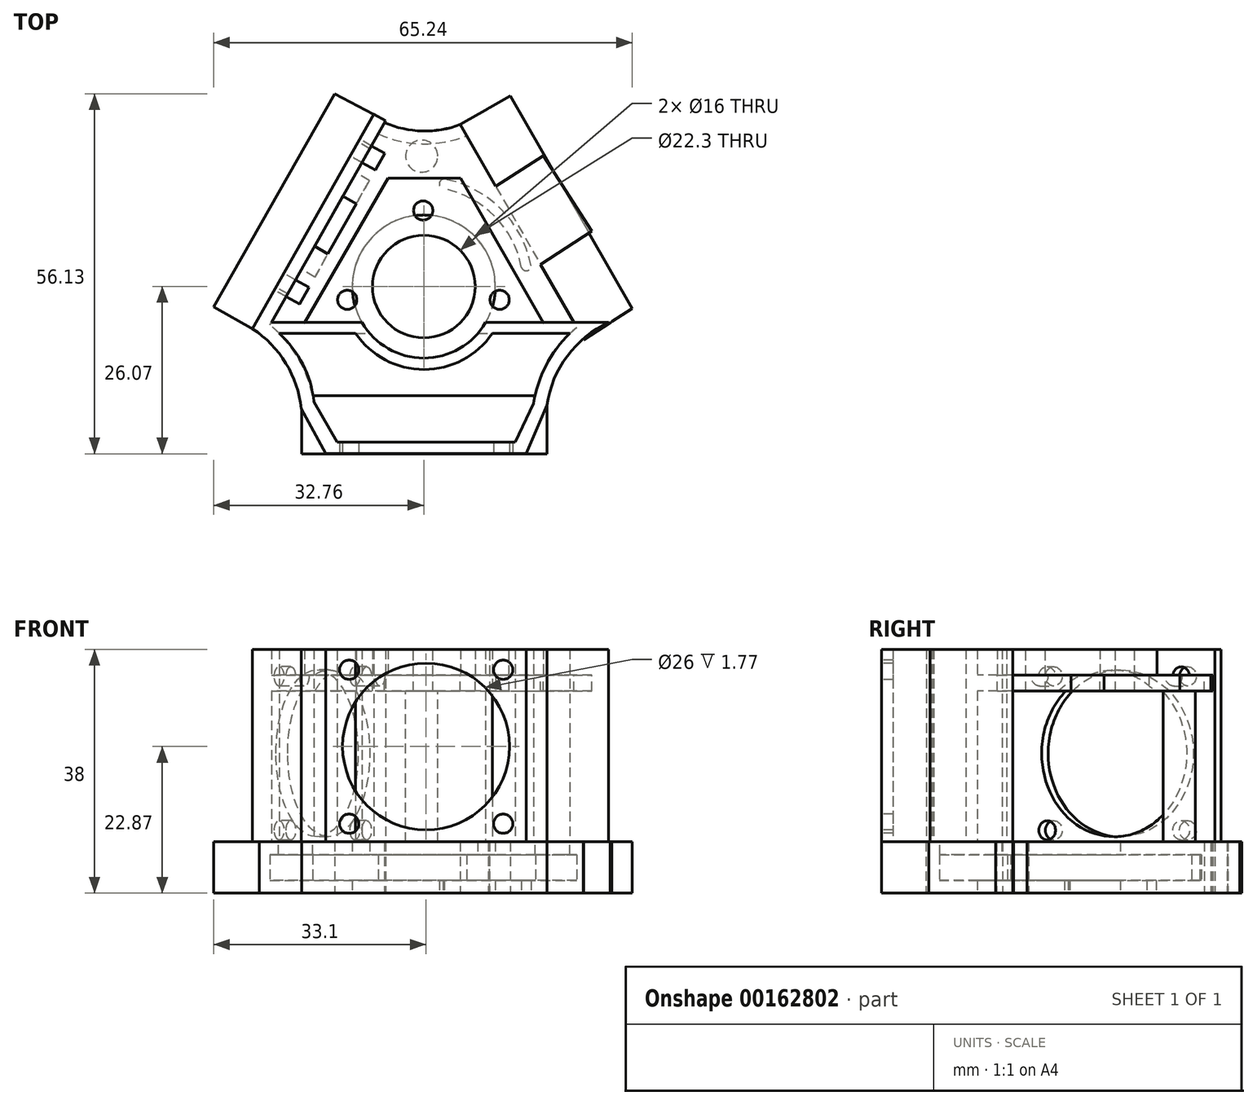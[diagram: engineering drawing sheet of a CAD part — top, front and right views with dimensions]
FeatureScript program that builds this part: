
annotation { "Feature Type Name" : "Feature", "Feature Type Description" : "" }
export const myFeature = defineFeature(function(context is Context, id is Id, definition is map)
    precondition{}
    {
        {
            var Q0;
            Q0=qCreatedBy(makeId("Top.planeOp"),FACE);
            var sketch = newSketch(context, id + "F0", { "sketchPlane" : qUnion([Q0])});
            skLineSegment(sketch, "E0", {"start": v(-28.93, -4.72) * mm, "end": v(-9.95, 28.39) * mm});
            skLineSegment(sketch, "E1", {"start": v(10.22, 28.39) * mm, "end": v(29.31, -5.05) * mm});
            skLineSegment(sketch, "E2", {"start": v(19.17, -21.87) * mm, "end": v(-19, -21.87) * mm});
            skArc(sketch, "E3", {"start": v(-9.95, 28.39) * mm, "mid": v(0.14, 24.72) * mm, "end": v(10.22, 28.39) * mm});
            skArc(sketch, "E4", {"start": v(-19, -21.87) * mm, "mid": v(-21.28, -11.74) * mm, "end": v(-28.93, -4.72) * mm});
            skArc(sketch, "E5", {"start": v(29.31, -5.05) * mm, "mid": v(21.38, -11.73) * mm, "end": v(19.17, -21.87) * mm});
            skSolve(sketch);
        }
        {
            var Q0;
            Q0 = qSketchRegion(id + "F0", true);
            extrude(context, id + "F1", {"entities" : qUnion([Q0]), "depth" : 8 * mm});
        }
        {
            var Q0;
            Q0=makeQuery(id+"F1.opExtrude","CAP_FACE",FACE,{"disambiguationData":[OSD([sQuery(id+"F0.wireOp",EDGE,"E0"),sQuery(id+"F0.wireOp",EDGE,"E1"),sQuery(id+"F0.wireOp",EDGE,"E2"),sQuery(id+"F0.wireOp",EDGE,"E3"),sQuery(id+"F0.wireOp",EDGE,"E4"),sQuery(id+"F0.wireOp",EDGE,"E5")])],"isStart":false});
            var Q1;
            Q1=makeQuery(id+"F1.opExtrude","SWEPT_BODY",BODY,{"disambiguationData":[OSD([sQuery(id+"F0.wireOp",EDGE,"E0"),sQuery(id+"F0.wireOp",EDGE,"E1"),sQuery(id+"F0.wireOp",EDGE,"E2"),sQuery(id+"F0.wireOp",EDGE,"E3"),sQuery(id+"F0.wireOp",EDGE,"E4"),sQuery(id+"F0.wireOp",EDGE,"E5")])]});
            shell(context, id + "F2", {"isHollow" : true, "entities" : qUnion([Q0]), "parts" : qUnion([Q1]), "thickness" : 2 * mm});
        }
        {
            var Q0;
            Q0=qCreatedBy(makeId("Top.planeOp"),FACE);
            var sketch = newSketch(context, id + "F3", { "sketchPlane" : qUnion([Q0])});
            skCircle(sketch, "E6", {"center": v(0, 0.47) * mm, "radius": 11.15 * mm});
            skSolve(sketch);
        }
        {
            var Q0;
            Q0 = qSketchRegion(id + "F3", true);
            extrude(context, id + "F4", {"entities" : qUnion([Q0]), "operationType" : NewBodyOperationType.REMOVE, "depth" : 8 * mm});
        }
        {
            var Q0;
            Q0=qCreatedBy(makeId("Top.planeOp"),FACE);
            var sketch = newSketch(context, id + "F5", { "sketchPlane" : qUnion([Q0])});
            skLineSegment(sketch, "E7.bottom", {"start": v(-19.03, -25.6) * mm, "end": v(19.17, -25.6) * mm});
            skLineSegment(sketch, "E7.top", {"start": v(-19.03, -16.6) * mm, "end": v(19.17, -16.6) * mm});
            skLineSegment(sketch, "E7.left", {"start": v(-19.03, -25.6) * mm, "end": v(-19.03, -16.6) * mm});
            skLineSegment(sketch, "E7.right", {"start": v(19.17, -25.6) * mm, "end": v(19.17, -16.6) * mm});
            skLineSegment(sketch, "E8", {"start": v(-5.95, 26.32) * mm, "end": v(-24.93, -7.14) * mm});
            skLineSegment(sketch, "E9", {"start": v(-24.93, -7.14) * mm, "end": v(-32.76, -2.7) * mm});
            skLineSegment(sketch, "E10", {"start": v(-32.76, -2.7) * mm, "end": v(-13.9, 30.53) * mm});
            skLineSegment(sketch, "E11", {"start": v(-13.9, 30.53) * mm, "end": v(-5.95, 26.32) * mm});
            skLineSegment(sketch, "E12", {"start": v(24.9, -7.82) * mm, "end": v(5.68, 25.75) * mm});
            skLineSegment(sketch, "E13", {"start": v(5.68, 25.75) * mm, "end": v(13.5, 30.22) * mm});
            skLineSegment(sketch, "E14", {"start": v(13.5, 30.22) * mm, "end": v(32.48, -2.93) * mm});
            skLineSegment(sketch, "E15", {"start": v(32.48, -2.93) * mm, "end": v(24.9, -7.82) * mm});
            skSolve(sketch);
        }
        {
            var Q0;
            Q0 = qSketchRegion(id + "F5", true);
            extrude(context, id + "F6", {"entities" : qUnion([Q0]), "operationType" : NewBodyOperationType.ADD, "depth" : 8 * mm});
        }
        {
            var Q0;
            Q0=qCreatedBy(makeId("Top.planeOp"),FACE);
            var sketch = newSketch(context, id + "F7", { "sketchPlane" : qUnion([Q0])});
            skArc(sketch, "E16", {"start": v(-3.14, 15.7) * mm, "mid": v(-11.4, 11.03) * mm, "end": v(-15.39, 2.41) * mm});
            skArc(sketch, "E17", {"start": v(-3.35, 17.2) * mm, "mid": v(-12.43, 12.13) * mm, "end": v(-16.86, 2.72) * mm});
            skArc(sketch, "E18", {"start": v(-3.68, -16.07) * mm, "mid": v(-2.82, -15.38) * mm, "end": v(-3.56, -14.55) * mm});
            skArc(sketch, "E19", {"start": v(3.62, -14.54) * mm, "mid": v(3.02, -15.33) * mm, "end": v(3.68, -16.07) * mm});
            skArc(sketch, "E20", {"start": v(-15.18, -2.6) * mm, "mid": v(-16.03, -2) * mm, "end": v(-16.67, -2.83) * mm});
            skArc(sketch, "E21", {"start": v(-16.86, 2.72) * mm, "mid": v(-16.08, 1.92) * mm, "end": v(-15.34, 2.76) * mm});
            skArc(sketch, "E22", {"start": v(16.53, -3.44) * mm, "mid": v(15.9, -2.57) * mm, "end": v(15.04, -3.22) * mm});
            skArc(sketch, "E23", {"start": v(15.22, 3.48) * mm, "mid": v(16.07, 2.94) * mm, "end": v(16.7, 3.73) * mm});
            skArc(sketch, "E24", {"start": v(-3.14, 15.7) * mm, "mid": v(-2.68, 16.53) * mm, "end": v(-3.35, 17.2) * mm});
            skArc(sketch, "E25", {"start": v(3.16, 17.23) * mm, "mid": v(2.41, 16.56) * mm, "end": v(2.99, 15.74) * mm});
            skArc(sketch, "E26.trimOffspring", {"start": v(-15.18, -2.59) * mm, "mid": v(-11, -10.38) * mm, "end": v(-3.26, -14.62) * mm});
            skArc(sketch, "E27.trimOffspring", {"start": v(-16.67, -2.83) * mm, "mid": v(-12.14, -11.37) * mm, "end": v(-3.68, -16.07) * mm});
            skArc(sketch, "E28.trimOffspring", {"start": v(16.7, 3.73) * mm, "mid": v(12, 12.57) * mm, "end": v(3.16, 17.23) * mm});
            skArc(sketch, "E29.trimOffspring", {"start": v(15.22, 3.48) * mm, "mid": v(10.98, 11.48) * mm, "end": v(2.99, 15.74) * mm});
            skArc(sketch, "E30.trimOffspring", {"start": v(3.62, -14.54) * mm, "mid": v(10.97, -10.42) * mm, "end": v(15.08, -3.06) * mm});
            skArc(sketch, "E31.trimOffspring", {"start": v(3.68, -16.07) * mm, "mid": v(11.92, -11.6) * mm, "end": v(16.53, -3.44) * mm});
            skSolve(sketch);
        }
        {
            var Q0;
            Q0 = qSketchRegion(id + "F7", true);
            extrude(context, id + "F8", {"entities" : qUnion([Q0]), "operationType" : NewBodyOperationType.REMOVE, "depth" : 2 * mm});
        }
        {
            var Q0;
            Q0=qCreatedBy(makeId("Top.planeOp"),FACE);
            cPlane(context, id + "F9", {"entities" : qUnion([Q0]), "cplaneType" : CPlaneType.OFFSET, "offset" : 8 * mm, "width" : 150 * mm, "height" : 150 * mm});
        }
        {
            var Q0;
            Q0=qCreatedBy(id+"F9.planeOp",FACE);
            var sketch = newSketch(context, id + "F10", { "sketchPlane" : qUnion([Q0])});
            skLineSegment(sketch, "E32.bottom", {"start": v(-22.63, -6.84) * mm, "end": v(22.76, -6.84) * mm});
            skLineSegment(sketch, "E32.top", {"start": v(-17.3, -16.53) * mm, "end": v(17.36, -16.53) * mm});
            skArc(sketch, "E33", {"start": v(-17.3, -16.53) * mm, "mid": v(-19.12, -11.22) * mm, "end": v(-22.63, -6.84) * mm});
            skArc(sketch, "E34", {"start": v(22.76, -6.84) * mm, "mid": v(19.34, -11.29) * mm, "end": v(17.36, -16.53) * mm});
            skSolve(sketch);
        }
        {
            var Q0;
            Q0 = qSketchRegion(id + "F10", true);
            extrude(context, id + "F11", {"entities" : qUnion([Q0]), "operationType" : NewBodyOperationType.REMOVE, "oppositeDirection" : true, "depth" : 2 * mm});
        }
        {
            var Q0;
            Q0=qCreatedBy(id+"F9.planeOp",FACE);
            var sketch = newSketch(context, id + "F12", { "sketchPlane" : qUnion([Q0])});
            skLineSegment(sketch, "E35", {"start": v(-23.76, -5.14) * mm, "end": v(-9.62, -5.14) * mm});
            skLineSegment(sketch, "E36", {"start": v(15.94, -25.57) * mm, "end": v(-15.28, -25.57) * mm});
            skLineSegment(sketch, "E37", {"start": v(19.18, -18.03) * mm, "end": v(15.94, -25.57) * mm});
            skLineSegment(sketch, "E38", {"start": v(-19.07, -18.6) * mm, "end": v(-15.28, -25.57) * mm});
            skArc(sketch, "E39", {"start": v(-9.62, -5.14) * mm, "mid": v(0, -10.69) * mm, "end": v(9.62, -5.14) * mm});
            skLineSegment(sketch, "E40.trimOffspring", {"start": v(9.62, -5.14) * mm, "end": v(28.8, -5.14) * mm});
            skArc(sketch, "E41", {"start": v(28.8, -5.14) * mm, "mid": v(22.35, -10.36) * mm, "end": v(19.18, -18.03) * mm});
            skLineSegment(sketch, "E42", {"start": v(-22.56, -6.83) * mm, "end": v(-10.63, -6.83) * mm});
            skArc(sketch, "E43", {"start": v(22.75, -6.83) * mm, "mid": v(19.04, -11.82) * mm, "end": v(17.1, -17.73) * mm});
            skArc(sketch, "E44", {"start": v(-17.11, -17.48) * mm, "mid": v(-18.87, -11.66) * mm, "end": v(-22.56, -6.83) * mm});
            skArc(sketch, "E45", {"start": v(-10.63, -6.83) * mm, "mid": v(0.02, -12.46) * mm, "end": v(10.67, -6.83) * mm});
            skLineSegment(sketch, "E46.trimOffspring", {"start": v(10.67, -6.83) * mm, "end": v(22.75, -6.83) * mm});
            skLineSegment(sketch, "E47", {"start": v(-13.5, -23.8) * mm, "end": v(14.25, -23.8) * mm});
            skLineSegment(sketch, "E48", {"start": v(14.25, -23.8) * mm, "end": v(17.1, -17.73) * mm});
            skLineSegment(sketch, "E49", {"start": v(-13.5, -23.8) * mm, "end": v(-17.11, -17.48) * mm});
            skLineSegment(sketch, "E50", {"start": v(-23.76, -5.14) * mm, "end": v(-5.95, 26.32) * mm});
            skLineSegment(sketch, "E51", {"start": v(-5.95, 26.32) * mm, "end": v(-7.83, 27.32) * mm});
            skLineSegment(sketch, "E52", {"start": v(-7.83, 27.32) * mm, "end": v(-26.7, -6.11) * mm});
            skArc(sketch, "E53", {"start": v(-19.07, -18.6) * mm, "mid": v(-21.5, -11.5) * mm, "end": v(-26.7, -6.11) * mm});
            skSolve(sketch);
        }
        {
            var Q0;
            Q0 = qSketchRegion(id + "F12", true);
            extrude(context, id + "F13", {"entities" : qUnion([Q0]), "operationType" : NewBodyOperationType.ADD, "depth" : 30 * mm});
        }
        {
            var Q0;
            Q0=qCreatedBy(makeId("Top.planeOp"),FACE);
            cPlane(context, id + "F14", {"entities" : qUnion([Q0]), "cplaneType" : CPlaneType.OFFSET, "offset" : 38 * mm, "width" : 150 * mm, "height" : 150 * mm});
        }
        {
            var Q0;
            Q0=qCreatedBy(id+"F14.planeOp",FACE);
            var sketch = newSketch(context, id + "F15", { "sketchPlane" : qUnion([Q0])});
            skLineSegment(sketch, "E54", {"start": v(24.75, -7.55) * mm, "end": v(24.83, -7.7) * mm});
            skLineSegment(sketch, "E55", {"start": v(24.83, -7.7) * mm, "end": v(24.83, -7.7) * mm});
            skLineSegment(sketch, "E56", {"start": v(19.2, -25.58) * mm, "end": v(19.17, -25.58) * mm});
            skLineSegment(sketch, "E57", {"start": v(-24.98, -7.28) * mm, "end": v(-24.98, -7.27) * mm});
            skArc(sketch, "E58.0", {"start": v(-19.03, -18.73) * mm, "mid": v(-20.9, -12.43) * mm, "end": v(-24.98, -7.28) * mm});
            skLineSegment(sketch, "E59.0", {"start": v(-19.03, -25.6) * mm, "end": v(-19.03, -25.58) * mm});
            skArc(sketch, "E60.0", {"start": v(24.83, -7.7) * mm, "mid": v(20.99, -12.42) * mm, "end": v(19.17, -18.23) * mm});
            skLineSegment(sketch, "E61.0", {"start": v(19.17, -25.6) * mm, "end": v(19.17, -25.58) * mm});
            skLineSegment(sketch, "E62.0", {"start": v(-5.95, 26.32) * mm, "end": v(-24.93, -7.14) * mm});
            skLineSegment(sketch, "E63.0", {"start": v(24.9, -7.82) * mm, "end": v(5.68, 25.75) * mm});
            skArc(sketch, "E64.0", {"start": v(-6.12, 26.02) * mm, "mid": v(-0.24, 24.72) * mm, "end": v(5.7, 25.73) * mm});
            skPoint(sketch, "E65.orphan", {"position": v(-9.95, 28.39) * mm});
            skPoint(sketch, "E66.orphan", {"position": v(10.22, 28.39) * mm});
            skPoint(sketch, "E67.orphan", {"position": v(-28.93, -4.72) * mm});
            skPoint(sketch, "E68.orphan", {"position": v(29.31, -5.05) * mm});
            skLineSegment(sketch, "E69.0", {"start": v(19.18, -18.03) * mm, "end": v(15.94, -25.57) * mm});
            skLineSegment(sketch, "E70.0", {"start": v(-19.07, -18.6) * mm, "end": v(-15.28, -25.57) * mm});
            skLineSegment(sketch, "E71.trimOffspring", {"start": v(19.17, -18.23) * mm, "end": v(19.17, -18.05) * mm});
            skPoint(sketch, "E72.orphan", {"position": v(19.17, -21.87) * mm});
            skPoint(sketch, "E73.orphan", {"position": v(19.17, -16.6) * mm});
            skLineSegment(sketch, "E74.trimOffspring", {"start": v(-19.03, -18.73) * mm, "end": v(-19.03, -18.68) * mm});
            skPoint(sketch, "E75.orphan", {"position": v(-19, -21.87) * mm});
            skPoint(sketch, "E76.orphan", {"position": v(-19.03, -16.6) * mm});
            skLineSegment(sketch, "E77.trimOffspring", {"start": v(-19.03, -25.58) * mm, "end": v(-19.04, -25.58) * mm});
            skSolve(sketch);
        }
        {
            var Q0;
            Q0=qCreatedBy(makeId("Top.planeOp"),FACE);
            cPlane(context, id + "F16", {"entities" : qUnion([Q0]), "cplaneType" : CPlaneType.OFFSET, "offset" : 34 * mm, "width" : 150 * mm, "height" : 150 * mm});
        }
        {
            var Q0;
            Q0=qCreatedBy(id+"F16.planeOp",FACE);
            var sketch = newSketch(context, id + "F17", { "sketchPlane" : qUnion([Q0])});
            skLineSegment(sketch, "E78.0", {"start": v(23.37, -5.14) * mm, "end": v(5.68, 25.75) * mm});
            skLineSegment(sketch, "E79.0", {"start": v(-23.76, -5.14) * mm, "end": v(-9.62, -5.14) * mm});
            skArc(sketch, "E80.0", {"start": v(-9.62, -5.14) * mm, "mid": v(0, -10.69) * mm, "end": v(9.62, -5.14) * mm});
            skLineSegment(sketch, "E81.0", {"start": v(9.62, -5.14) * mm, "end": v(28.8, -5.14) * mm});
            skArc(sketch, "E82.0", {"start": v(-6.12, 26.02) * mm, "mid": v(-0.24, 24.72) * mm, "end": v(5.7, 25.73) * mm});
            skPoint(sketch, "E83.orphan", {"position": v(-9.95, 28.39) * mm});
            skPoint(sketch, "E84.orphan", {"position": v(-5.95, 26.32) * mm});
            skPoint(sketch, "E85.orphan", {"position": v(10.22, 28.39) * mm});
            skPoint(sketch, "E86.orphan", {"position": v(24.9, -7.82) * mm});
            skPoint(sketch, "E87.0.end.orphan", {"position": v(-24.93, -7.14) * mm});
            skLineSegment(sketch, "E88", {"start": v(-6.12, 26.02) * mm, "end": v(-23.76, -5.14) * mm});
            skSolve(sketch);
        }
        {
            var Q0;
            Q0 = qSketchRegion(id + "F17", true);
            extrude(context, id + "F18", {"entities" : qUnion([Q0]), "operationType" : NewBodyOperationType.ADD, "oppositeDirection" : true, "depth" : 2.5 * mm});
        }
        {
            var Q0;
            Q0=qCreatedBy(id+"F16.planeOp",FACE);
            var sketch = newSketch(context, id + "F19", { "sketchPlane" : qUnion([Q0])});
            skCircle(sketch, "E89", {"center": v(0, 0.47) * mm, "radius": 8 * mm});
            skSolve(sketch);
        }
        {
            var Q0;
            Q0 = qSketchRegion(id + "F19", true);
            extrude(context, id + "F20", {"entities" : qUnion([Q0]), "operationType" : NewBodyOperationType.REMOVE, "oppositeDirection" : true, "depth" : 2.5 * mm});
        }
        {
            var Q0;
            Q0=qCreatedBy(id+"F16.planeOp",FACE);
            var sketch = newSketch(context, id + "F21", { "sketchPlane" : qUnion([Q0])});
            skCircle(sketch, "E90.0", {"center": v(0, 0.47) * mm, "radius": 8 * mm});
            skArc(sketch, "E91.0", {"start": v(-9.62, -5.14) * mm, "mid": v(0, -10.69) * mm, "end": v(9.62, -5.14) * mm});
            skLineSegment(sketch, "E92", {"start": v(-5.55, 17.34) * mm, "end": v(-18.62, -5.15) * mm});
            skLineSegment(sketch, "E93", {"start": v(-18.62, -5.15) * mm, "end": v(-9.62, -5.14) * mm});
            skLineSegment(sketch, "E94", {"start": v(-5.55, 17.34) * mm, "end": v(5.74, 17.34) * mm});
            skLineSegment(sketch, "E95", {"start": v(5.74, 17.34) * mm, "end": v(18.62, -5.15) * mm});
            skLineSegment(sketch, "E96", {"start": v(18.62, -5.15) * mm, "end": v(9.62, -5.14) * mm});
            skPoint(sketch, "E97", {"position": v(0, 12.4) * mm});
            skPoint(sketch, "E98", {"position": v(12.32, -1.74) * mm});
            skPoint(sketch, "E99", {"position": v(-12.04, -1.74) * mm});
            skSolve(sketch);
        }
        {
            var Q0;
            Q0 = qSketchRegion(id + "F21", true);
            extrude(context, id + "F22", {"entities" : qUnion([Q0]), "depth" : 4 * mm});
        }
        {
            var Q0;
            Q0=qCreatedBy(id+"F16.planeOp",FACE);
            var sketch = newSketch(context, id + "F23", { "sketchPlane" : qUnion([Q0])});
            skCircle(sketch, "E100", {"center": v(-0.34, 20.8) * mm, "radius": 2.5 * mm});
            skSolve(sketch);
        }
        {
            var Q0;
            Q0 = qSketchRegion(id + "F23", true);
            var Q1;
            {var subQ4=sQuery(id+"F0.wireOp",EDGE,"E1");var subQ5=sQuery(id+"F5.wireOp",EDGE,"E14");var subQ6=sQuery(id+"F5.wireOp",EDGE,"E12");var subQ7=sQuery(id+"F5.wireOp",EDGE,"E15");var subQ8=sQuery(id+"F0.wireOp",EDGE,"E5");var subQ9=sQuery(id+"F0.wireOp",EDGE,"E3");var subQ10=sQuery(id+"F5.wireOp",EDGE,"E13");var subQ11=sQuery(id+"F0.wireOp",EDGE,"E4");var subQ12=sQuery(id+"F0.wireOp",EDGE,"E2");var subQ13=sQuery(id+"F0.wireOp",EDGE,"E0");var subQ14=makeQuery(id+"F1.opExtrude","CAP_FACE",FACE,{"disambiguationData":[OSD([subQ13,subQ4,subQ12,subQ9,subQ11,subQ8])],"isStart":false});Q1=makeQuery(id+"F13.boolean.opBoolean","SPLIT",FACE,{"disambiguationData":[TD([makeQuery(id+"F1.opExtrude","SWEPT_FACE",FACE,{"disambiguationData":[OSD([subQ4])]})])],"derivedFrom":makeQuery(id+"F6.boolean.opBoolean","MERGE",FACE,{"derivedFrom":[subQ14,makeQuery(id+"F6.opExtrude","CAP_FACE",FACE,{"disambiguationData":[OSD([sQuery(id+"F5.wireOp",EDGE,"E7.bottom"),sQuery(id+"F5.wireOp",EDGE,"E7.top"),sQuery(id+"F5.wireOp",EDGE,"E7.left"),sQuery(id+"F5.wireOp",EDGE,"E7.right")])],"isStart":false}),makeQuery(id+"F6.opExtrude","CAP_FACE",FACE,{"disambiguationData":[OSD([sQuery(id+"F5.wireOp",EDGE,"E8"),sQuery(id+"F5.wireOp",EDGE,"E9"),sQuery(id+"F5.wireOp",EDGE,"E10"),sQuery(id+"F5.wireOp",EDGE,"E11")])],"isStart":false}),makeQuery(id+"F6.opExtrude","CAP_FACE",FACE,{"disambiguationData":[OSD([subQ6,subQ10,subQ5,subQ7])],"isStart":false})]})});}
            extrude(context, id + "F24", {"entities" : qUnion([Q0]), "operationType" : NewBodyOperationType.ADD, "endBound" : BoundingType.UP_TO_SURFACE, "oppositeDirection" : true, "endBoundEntityFace" : qUnion([Q1]), "depth" : 25 * mm});
        }
        {
            var Q0;
            Q0=makeQuery(id+"F22.opExtrude","CAP_FACE",FACE,{"disambiguationData":[OSD([sQuery(id+"F21.wireOp",EDGE,"E90.0"),sQuery(id+"F21.wireOp",EDGE,"E91.0"),sQuery(id+"F21.wireOp",EDGE,"E92"),sQuery(id+"F21.wireOp",EDGE,"E93"),sQuery(id+"F21.wireOp",EDGE,"E94"),sQuery(id+"F21.wireOp",EDGE,"E95"),sQuery(id+"F21.wireOp",EDGE,"E96")])],"isStart":false});
            var sketch = newSketch(context, id + "F25", { "sketchPlane" : qUnion([Q0])});
            skPoint(sketch, "E101", {"position": v(-0.11, 12.33) * mm});
            skPoint(sketch, "E102", {"position": v(11.81, -1.6) * mm});
            skPoint(sketch, "E103", {"position": v(-11.94, -1.6) * mm});
            skSolve(sketch);
        }
        {
            var Q0;
            Q0=sQuery(id+"F25.wireOp",VERTEX,"E101");
            var Q1;
            Q1=sQuery(id+"F25.wireOp",VERTEX,"E103");
            var Q2;
            Q2=sQuery(id+"F25.wireOp",VERTEX,"E102");
            var Q3;
            Q3=makeQuery(id+"F22.opExtrude","SWEPT_BODY",BODY,{"disambiguationData":[OSD([sQuery(id+"F21.wireOp",EDGE,"E90.0"),sQuery(id+"F21.wireOp",EDGE,"E91.0"),sQuery(id+"F21.wireOp",EDGE,"E92"),sQuery(id+"F21.wireOp",EDGE,"E93"),sQuery(id+"F21.wireOp",EDGE,"E94"),sQuery(id+"F21.wireOp",EDGE,"E95"),sQuery(id+"F21.wireOp",EDGE,"E96")])]});
            var Q4;
            Q4=makeQuery(id+"F1.opExtrude","SWEPT_BODY",BODY,{"disambiguationData":[OSD([sQuery(id+"F0.wireOp",EDGE,"E0"),sQuery(id+"F0.wireOp",EDGE,"E1"),sQuery(id+"F0.wireOp",EDGE,"E2"),sQuery(id+"F0.wireOp",EDGE,"E3"),sQuery(id+"F0.wireOp",EDGE,"E4"),sQuery(id+"F0.wireOp",EDGE,"E5")])]});
            hole(context, id + "F26", {"style" : HoleStyle.SIMPLE, "endStyle" : HoleEndStyle.BLIND, "holeDiameter" : 3 * mm, "holeDepth" : 8 * mm, "locations" : qUnion([Q0, Q1, Q2]), "scope" : qUnion([Q3, Q4])});
        }
        {
            var Q0;
            Q0=qCreatedBy(id+"F16.planeOp",FACE);
            var sketch = newSketch(context, id + "F27", { "sketchPlane" : qUnion([Q0])});
            skLineSegment(sketch, "E104", {"start": v(8.51, 14.34) * mm, "end": v(18.59, 20.86) * mm});
            skLineSegment(sketch, "E105", {"start": v(18.59, 20.86) * mm, "end": v(26.2, 9.1) * mm});
            skLineSegment(sketch, "E106", {"start": v(26.2, 9.1) * mm, "end": v(16.11, 2.59) * mm});
            skLineSegment(sketch, "E107", {"start": v(16.11, 2.59) * mm, "end": v(8.51, 14.34) * mm});
            skSolve(sketch);
        }
        {
            var Q0;
            Q0 = qSketchRegion(id + "F27", true);
            var Q1;
            Q1=sQuery(id+"F27.wireOp",EDGE,"E104");
            var Q2;
            Q2=sQuery(id+"F27.wireOp",EDGE,"E106");
            var Q3;
            Q3=sQuery(id+"F27.wireOp",EDGE,"E107");
            var Q4;
            Q4=sQuery(id+"F27.wireOp",EDGE,"E105");
            extrude(context, id + "F28", {"entities" : qUnion([Q0]), "operationType" : NewBodyOperationType.ADD, "surfaceEntities" : qUnion([Q1, Q2, Q3, Q4]), "oppositeDirection" : true, "depth" : 2.5 * mm});
        }
        {
            var Q0;
            Q0=makeQuery(id+"F13.opExtrude","SWEPT_FACE",FACE,{"disambiguationData":[OSD([sQuery(id+"F12.wireOp",EDGE,"E36")])]});
            var sketch = newSketch(context, id + "F29", { "sketchPlane" : qUnion([Q0])});
            skLineSegment(sketch, "E108.bottom", {"start": v(-11.64, 34.83) * mm, "end": v(12.36, 34.83) * mm, "construction": true});
            skLineSegment(sketch, "E108.top", {"start": v(-11.64, 10.83) * mm, "end": v(12.36, 10.83) * mm, "construction": true});
            skLineSegment(sketch, "E108.left", {"start": v(-11.64, 34.83) * mm, "end": v(-11.64, 10.83) * mm, "construction": true});
            skLineSegment(sketch, "E108.right", {"start": v(12.36, 34.83) * mm, "end": v(12.36, 10.83) * mm, "construction": true});
            skCircle(sketch, "E109", {"center": v(-11.64, 34.83) * mm, "radius": 1.5 * mm});
            skCircle(sketch, "E110", {"center": v(12.36, 34.83) * mm, "radius": 1.5 * mm});
            skCircle(sketch, "E111", {"center": v(-11.64, 10.83) * mm, "radius": 1.5 * mm});
            skCircle(sketch, "E112", {"center": v(12.36, 10.83) * mm, "radius": 1.5 * mm});
            skCircle(sketch, "E113", {"center": v(0.34, 22.87) * mm, "radius": 13 * mm});
            skSolve(sketch);
        }
        {
            var Q0;
            Q0 = qSketchRegion(id + "F29", true);
            extrude(context, id + "F30", {"entities" : qUnion([Q0]), "operationType" : NewBodyOperationType.REMOVE, "endBound" : BoundingType.UP_TO_NEXT, "oppositeDirection" : true, "depth" : 25 * mm});
        }
        {
            var Q0;
            Q0=makeQuery(id+"F13.opExtrude","SWEPT_FACE",FACE,{"disambiguationData":[OSD([sQuery(id+"F12.wireOp",EDGE,"E52")])]});
            var sketch = newSketch(context, id + "F31", { "sketchPlane" : qUnion([Q0])});
            skLineSegment(sketch, "E114.bottom", {"start": v(10.01, 9.8) * mm, "end": v(-13.99, 9.8) * mm, "construction": true});
            skLineSegment(sketch, "E114.top", {"start": v(10.01, 33.8) * mm, "end": v(-13.99, 33.8) * mm, "construction": true});
            skLineSegment(sketch, "E114.left", {"start": v(10.01, 9.8) * mm, "end": v(10.01, 33.8) * mm, "construction": true});
            skLineSegment(sketch, "E114.right", {"start": v(-13.99, 9.8) * mm, "end": v(-13.99, 33.8) * mm, "construction": true});
            skPoint(sketch, "E114.middle", {"position": v(-1.99, 21.8) * mm});
            skCircle(sketch, "E115", {"center": v(-13.99, 33.8) * mm, "radius": 1.5 * mm});
            skCircle(sketch, "E116", {"center": v(10.01, 33.8) * mm, "radius": 1.5 * mm});
            skCircle(sketch, "E117", {"center": v(10.01, 9.8) * mm, "radius": 1.5 * mm});
            skCircle(sketch, "E118", {"center": v(-13.99, 9.8) * mm, "radius": 1.5 * mm});
            skCircle(sketch, "E119", {"center": v(-1.99, 21.8) * mm, "radius": 13 * mm});
            skSolve(sketch);
        }
        {
            var Q0;
            Q0 = qSketchRegion(id + "F31", true);
            extrude(context, id + "F32", {"entities" : qUnion([Q0]), "operationType" : NewBodyOperationType.REMOVE, "oppositeDirection" : true, "depth" : 4.5 * mm});
        }
        {
            var Q0;
            Q0=qSketchRegion(id+"F7",true);
            var Q1;
            Q1=sQuery(id+"F7.wireOp",EDGE,"657ce379-fd31-4219-99dd-da7bc6678c47.trimOffspring");
            var Q2;
            Q2=sQuery(id+"F7.wireOp",EDGE,"61bfabfc-1287-4681-8809-1c9ec826a01b.trimOffspring");
            var Q3;
            Q3=sQuery(id+"F7.wireOp",EDGE,"d9df856a-e3e1-4b30-ae25-94071e8a40d7.trimOffspring");
            var Q4;
            Q4=sQuery(id+"F7.wireOp",EDGE,"8c14bfa4-37d8-4f89-b281-bf2e3e316ce7");
            var Q5;
            Q5=sQuery(id+"F7.wireOp",EDGE,"024fcc8a-74a1-49de-a56b-3ee84f62e903");
            var Q6;
            Q6=sQuery(id+"F7.wireOp",EDGE,"7ed61add-e6c4-498b-abee-b3ce91ed069e.trimOffspring");
            var Q7;
            Q7=sQuery(id+"F7.wireOp",EDGE,"0a75f7fa-2392-40e4-aa4a-17d126546641.trimOffspring");
            var Q8;
            Q8=sQuery(id+"F7.wireOp",EDGE,"3ebe3453-0fd6-4324-8ad3-ee03ab6c34e6.trimOffspring");
            var Q9;
            Q9=sQuery(id+"F7.wireOp",EDGE,"bb5ed3d1-6caf-45be-bb83-1f2de96645e3");
            var Q10;
            Q10=sQuery(id+"F7.wireOp",EDGE,"72226a40-40ef-4773-9bd7-ac5483c8a1ee");
            var Q11;
            Q11=sQuery(id+"F7.wireOp",EDGE,"712d4b47-e79a-45a8-ac87-298464db6401");
            var Q12;
            Q12=sQuery(id+"F7.wireOp",EDGE,"47ae149c-1c11-4b30-b7cc-de5eb1596486");
            var Q13;
            Q13=sQuery(id+"F7.wireOp",EDGE,"fd097cd4-3339-4943-a8e7-178eac5bea0e");
            var Q14;
            Q14=sQuery(id+"F7.wireOp",EDGE,"09241623-0723-4807-a3de-83c01c0f3ae4");
            var Q15;
            Q15=sQuery(id+"F7.wireOp",EDGE,"5aa8b615-d2aa-4331-9156-7ead240934e3");
            var Q16;
            Q16=sQuery(id+"F7.wireOp",EDGE,"c76e4508-1ab7-4ba4-8cb1-0699f6b43202");
            extrude(context, id + "F33", {"entities" : qUnion([Q0]), "operationType" : NewBodyOperationType.REMOVE, "surfaceEntities" : qUnion([Q1, Q2, Q3, Q4, Q5, Q6, Q7, Q8, Q9, Q10, Q11, Q12, Q13, Q14, Q15, Q16]), "endBound" : BoundingType.UP_TO_NEXT, "depth" : 25 * mm});
        }
    });
